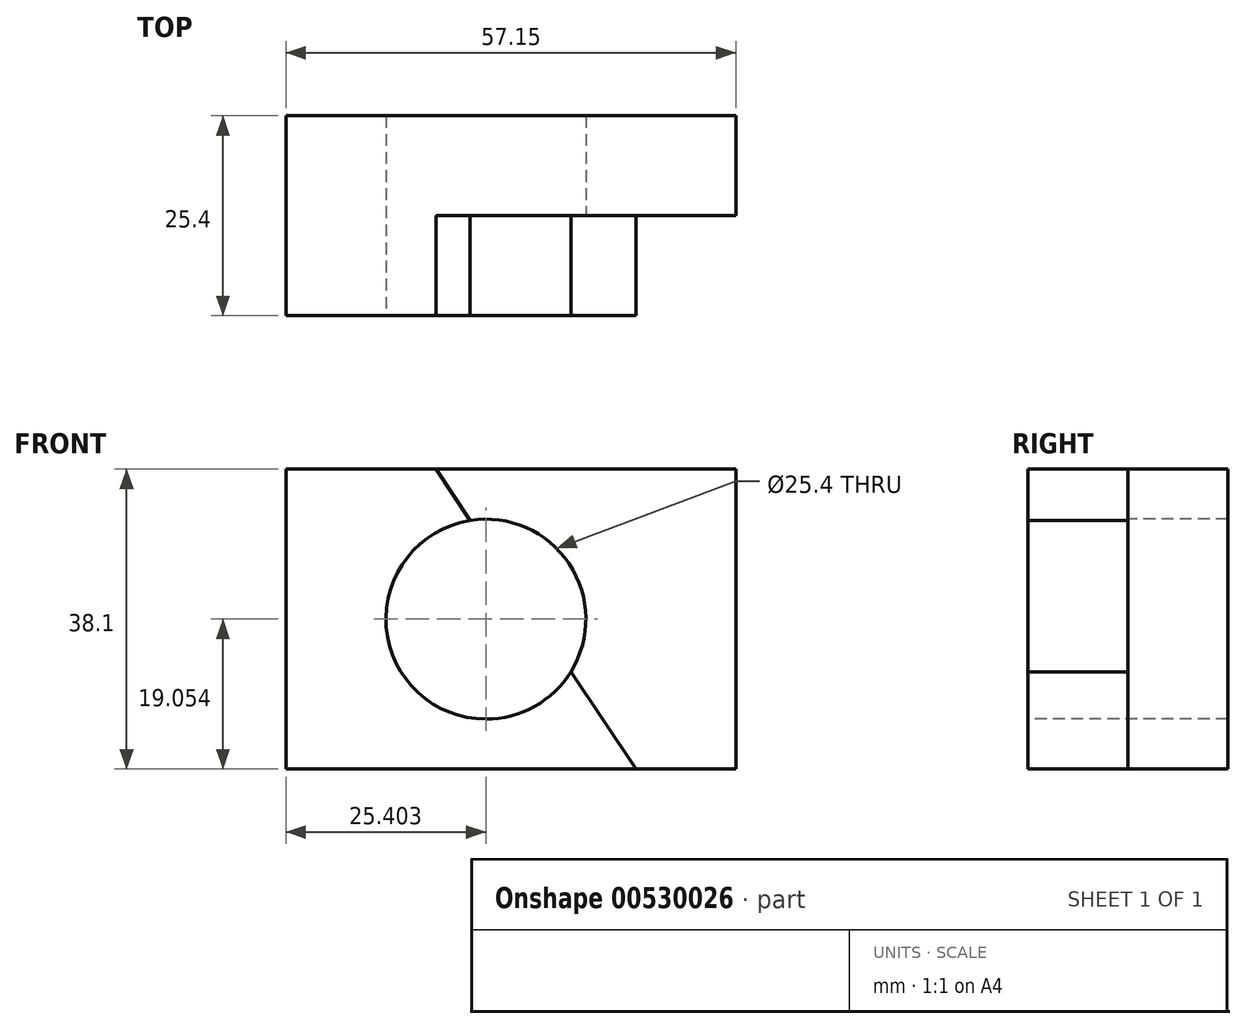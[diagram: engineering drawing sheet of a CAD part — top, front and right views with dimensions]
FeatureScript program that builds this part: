
annotation { "Feature Type Name" : "Feature", "Feature Type Description" : "" }
export const myFeature = defineFeature(function(context is Context, id is Id, definition is map)
    precondition{}
    {
        {
            var Q0;
            Q0=qCreatedBy(makeId("Front.planeOp"),FACE);
            var sketch = newSketch(context, id + "F0", { "sketchPlane" : qUnion([Q0])});
            skLineSegment(sketch, "E0.bottom", {"start": v(-35.35, 34.04) * mm, "end": v(21.8, 34.04) * mm});
            skLineSegment(sketch, "E0.top", {"start": v(-35.35, -4.06) * mm, "end": v(21.8, -4.06) * mm});
            skLineSegment(sketch, "E0.left", {"start": v(-35.35, 34.04) * mm, "end": v(-35.35, -4.06) * mm});
            skLineSegment(sketch, "E0.right", {"start": v(21.8, 34.04) * mm, "end": v(21.8, -4.06) * mm});
            skSolve(sketch);
        }
        {
            var Q0;
            Q0=makeQuery(id+"F0.imprint","IMPRINT",FACE,{"disambiguationData":[TD([[makeQuery(id+"F0.imprint","IMPRINT",EDGE,{"derivedFrom":sQuery(id+"F0.wireOp",EDGE,"E0.bottom")}),-1.0]])]});
            extrude(context, id + "F1", {"entities" : qUnion([Q0]), "depth" : 25.4 * mm, "offsetDistance" : 25.4 * mm});
        }
        {
            var Q0;
            Q0=makeQuery(id+"F1.opExtrude","CAP_FACE",FACE,{"disambiguationData":[OSD([sQuery(id+"F0.wireOp",EDGE,"E0.bottom"),sQuery(id+"F0.wireOp",EDGE,"E0.top"),sQuery(id+"F0.wireOp",EDGE,"E0.left"),sQuery(id+"F0.wireOp",EDGE,"E0.right")])],"isStart":false});
            var sketch = newSketch(context, id + "F2", { "sketchPlane" : qUnion([Q0])});
            skLineSegment(sketch, "E1", {"start": v(-16.3, 34.04) * mm, "end": v(9.1, -4.06) * mm});
            skLineSegment(sketch, "E2", {"start": v(-16.3, 34.04) * mm, "end": v(21.8, 34.04) * mm});
            skLineSegment(sketch, "E3", {"start": v(21.8, 34.04) * mm, "end": v(21.8, -4.06) * mm});
            skLineSegment(sketch, "E4", {"start": v(9.1, -4.06) * mm, "end": v(21.8, -4.06) * mm});
            skSolve(sketch);
        }
        {
            var Q0;
            Q0=makeQuery(id+"F2.imprint","IMPRINT",FACE,{"disambiguationData":[TD([[makeQuery(id+"F2.imprint","IMPRINT",EDGE,{"derivedFrom":sQuery(id+"F2.wireOp",EDGE,"E1")}),1.0]])]});
            extrude(context, id + "F3", {"entities" : qUnion([Q0]), "operationType" : NewBodyOperationType.REMOVE, "oppositeDirection" : true, "depth" : 12.7 * mm, "offsetDistance" : 25.4 * mm});
        }
        {
            var Q0;
            Q0=makeQuery(id+"F1.opExtrude","CAP_FACE",FACE,{"disambiguationData":[OSD([sQuery(id+"F0.wireOp",EDGE,"E0.bottom"),sQuery(id+"F0.wireOp",EDGE,"E0.top"),sQuery(id+"F0.wireOp",EDGE,"E0.left"),sQuery(id+"F0.wireOp",EDGE,"E0.right")])],"isStart":false});
            var sketch = newSketch(context, id + "F4", { "sketchPlane" : qUnion([Q0])});
            skCircle(sketch, "E5", {"center": v(-9.95, 15) * mm, "radius": 12.7 * mm});
            skSolve(sketch);
        }
        {
            var Q0;
            {var subQ0=sQuery(id+"F4.wireOp",EDGE,"E5");var subQ1=makeQuery(id+"F3.boolean.opBoolean","COPY",EDGE,{"derivedFrom":makeQuery(id+"F3.opExtrude","CAP_EDGE",EDGE,{"disambiguationData":[OSD([sQuery(id+"F2.wireOp",EDGE,"E1")])],"isStart":true})});var subQ2=makeQuery(id+"F4.imprint","INTERSECT",VERTEX,{"disambiguationData":[OD(0.0)],"derivedFrom":[subQ1,subQ0]});Q0=makeQuery(id+"F4.imprint","IMPRINT",FACE,{"disambiguationData":[TD([[makeQuery(id+"F4.imprint","IMPRINT",EDGE,{"disambiguationData":[TD([[subQ2,-1.0]])],"derivedFrom":subQ0}),1.0]])]});}
            var Q1;
            {var subQ0=sQuery(id+"F4.wireOp",EDGE,"E5");var subQ1=makeQuery(id+"F3.boolean.opBoolean","COPY",EDGE,{"derivedFrom":makeQuery(id+"F3.opExtrude","CAP_EDGE",EDGE,{"disambiguationData":[OSD([sQuery(id+"F2.wireOp",EDGE,"E1")])],"isStart":true})});var subQ2=makeQuery(id+"F4.imprint","INTERSECT",VERTEX,{"disambiguationData":[OD(0.0)],"derivedFrom":[subQ1,subQ0]});Q1=makeQuery(id+"F4.imprint","IMPRINT",FACE,{"disambiguationData":[TD([[makeQuery(id+"F4.imprint","IMPRINT",EDGE,{"disambiguationData":[TD([[subQ2,1.0]])],"derivedFrom":subQ0}),1.0]])]});}
            extrude(context, id + "F5", {"entities" : qUnion([Q0, Q1]), "operationType" : NewBodyOperationType.REMOVE, "endBound" : BoundingType.THROUGH_ALL, "oppositeDirection" : true, "depth" : 25.4 * mm, "offsetDistance" : 25.4 * mm});
        }
    });
